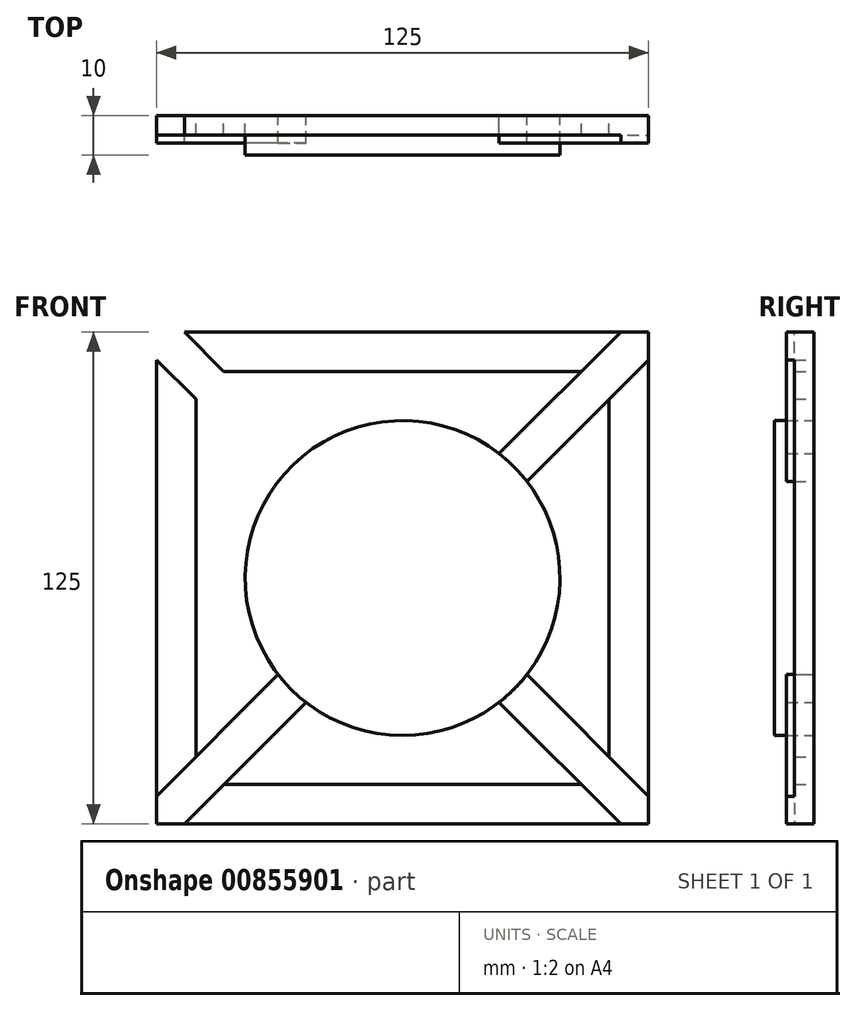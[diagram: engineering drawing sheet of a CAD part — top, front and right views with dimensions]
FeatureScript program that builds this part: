
annotation { "Feature Type Name" : "Feature", "Feature Type Description" : "" }
export const myFeature = defineFeature(function(context is Context, id is Id, definition is map)
    precondition{}
    {
        {
            var Q0;
            Q0=qCreatedBy(makeId("Front.planeOp"),FACE);
            var sketch = newSketch(context, id + "F0", { "sketchPlane" : qUnion([Q0])});
            skLineSegment(sketch, "E0", {"start": v(50.2, 9.17) * mm, "end": v(50.2, -90.83) * mm});
            skLineSegment(sketch, "E1", {"start": v(50.2, -90.83) * mm, "end": v(-74.8, -90.83) * mm});
            skLineSegment(sketch, "E2", {"start": v(-74.8, -90.83) * mm, "end": v(-74.8, 34.17) * mm});
            skLineSegment(sketch, "E3", {"start": v(-74.8, 34.17) * mm, "end": v(50.2, 34.17) * mm});
            skLineSegment(sketch, "E4", {"start": v(50.2, 34.17) * mm, "end": v(50.2, 9.17) * mm});
            skPoint(sketch, "E5.endSnap0", {"position": v(-37.4, -38.1) * mm});
            skLineSegment(sketch, "E6", {"start": v(-74.8, -28.33) * mm, "end": v(-64.8, -28.33) * mm});
            skLineSegment(sketch, "E7", {"start": v(0, 34.17) * mm, "end": v(0, 24.17) * mm});
            skLineSegment(sketch, "E8", {"start": v(0, -90.83) * mm, "end": v(0, -80.83) * mm});
            skLineSegment(sketch, "E9", {"start": v(50.2, 0) * mm, "end": v(40.2, 0) * mm});
            skLineSegment(sketch, "E10", {"start": v(-12.3, -28.33) * mm, "end": v(-12.3, 34.17) * mm});
            skCircle(sketch, "E11", {"center": v(-12.3, -28.33) * mm, "radius": 40 * mm});
            skPoint(sketch, "E12.endSnap0", {"position": v(25.1, -80.83) * mm});
            skLineSegment(sketch, "E13", {"start": v(-44.16, 3.54) * mm, "end": v(-40.63, 7.07) * mm});
            skLineSegment(sketch, "E14", {"start": v(-44.16, 3.54) * mm, "end": v(-47.7, 0) * mm});
            skLineSegment(sketch, "E15", {"start": v(-44.16, -60.2) * mm, "end": v(-40.63, -63.74) * mm});
            skLineSegment(sketch, "E16", {"start": v(-44.16, -60.2) * mm, "end": v(-47.7, -56.67) * mm});
            skLineSegment(sketch, "E17", {"start": v(28.89, -69.52) * mm, "end": v(25.35, -73.05) * mm});
            skLineSegment(sketch, "E18", {"start": v(28.89, -69.52) * mm, "end": v(32.42, -65.98) * mm});
            skLineSegment(sketch, "E19", {"start": v(27.75, 11.72) * mm, "end": v(31.3, 8.18) * mm});
            skLineSegment(sketch, "E20", {"start": v(27.75, 11.72) * mm, "end": v(24.22, 15.25) * mm});
            skLineSegment(sketch, "E21", {"start": v(-40.63, -63.74) * mm, "end": v(-67.72, -90.83) * mm});
            skLineSegment(sketch, "E22", {"start": v(-47.7, -56.67) * mm, "end": v(-74.8, -83.76) * mm});
            skLineSegment(sketch, "E23", {"start": v(25.35, -73.05) * mm, "end": v(43.13, -90.83) * mm});
            skLineSegment(sketch, "E24", {"start": v(32.42, -65.98) * mm, "end": v(50.2, -83.76) * mm});
            skLineSegment(sketch, "E25", {"start": v(31.3, 8.18) * mm, "end": v(19.3, -3.8) * mm});
            skLineSegment(sketch, "E26", {"start": v(31.3, 8.18) * mm, "end": v(50.2, 27.1) * mm});
            skLineSegment(sketch, "E27", {"start": v(24.22, 15.25) * mm, "end": v(12.23, 3.27) * mm});
            skLineSegment(sketch, "E28", {"start": v(24.22, 15.25) * mm, "end": v(43.13, 34.17) * mm});
            skLineSegment(sketch, "E29", {"start": v(-47.7, -56.67) * mm, "end": v(-43.9, -52.86) * mm});
            skLineSegment(sketch, "E30", {"start": v(-40.63, -63.74) * mm, "end": v(-36.82, -59.93) * mm});
            skLineSegment(sketch, "E31", {"start": v(32.42, -65.98) * mm, "end": v(19.3, -52.86) * mm});
            skLineSegment(sketch, "E32", {"start": v(25.35, -73.05) * mm, "end": v(12.23, -59.93) * mm});
            skLineSegment(sketch, "E33", {"start": v(-47.7, 0) * mm, "end": v(-74.8, 27.1) * mm});
            skLineSegment(sketch, "E34", {"start": v(-40.63, 7.07) * mm, "end": v(-67.72, 34.17) * mm});
            skLineSegment(sketch, "E35", {"start": v(-47.7, 0) * mm, "end": v(-40.63, 7.07) * mm});
            skLineSegment(sketch, "E36", {"start": v(-40.63, 7.07) * mm, "end": v(-36.82, 3.27) * mm});
            skLineSegment(sketch, "E37", {"start": v(-64.8, -28.33) * mm, "end": v(-64.8, 17.1) * mm});
            skLineSegment(sketch, "E38", {"start": v(-64.8, -28.33) * mm, "end": v(-64.8, -73.76) * mm});
            skLineSegment(sketch, "E39", {"start": v(0, -80.83) * mm, "end": v(-57.72, -80.83) * mm});
            skLineSegment(sketch, "E40", {"start": v(0, -80.83) * mm, "end": v(33.13, -80.83) * mm});
            skLineSegment(sketch, "E41", {"start": v(40.2, 0) * mm, "end": v(40.2, -73.76) * mm});
            skLineSegment(sketch, "E42", {"start": v(40.2, 0) * mm, "end": v(40.2, 17.1) * mm});
            skLineSegment(sketch, "E43", {"start": v(0, 24.17) * mm, "end": v(33.13, 24.17) * mm});
            skLineSegment(sketch, "E44", {"start": v(0, 24.17) * mm, "end": v(-57.72, 24.17) * mm});
            skLineSegment(sketch, "E45", {"start": v(-44.16, -3.54) * mm, "end": v(-43.9, -3.8) * mm});
            skLineSegment(sketch, "E46", {"start": v(-43.9, -3.8) * mm, "end": v(-43.9, -3.8) * mm});
            skLineSegment(sketch, "E47", {"start": v(-47.7, 0) * mm, "end": v(-44.16, -3.54) * mm});
            skSolve(sketch);
        }
        {
            var Q0;
            {var subQ0=sQuery(id+"F0.wireOp",EDGE,"E11");var subQ5=makeQuery(id+"F0.imprint","INTERSECT",VERTEX,{"derivedFrom":[subQ0,sQuery(id+"F0.wireOp",EDGE,"E25")]});Q0=makeQuery(id+"F0.imprint","IMPRINT",FACE,{"disambiguationData":[TD([[makeQuery(id+"F0.imprint","IMPRINT",EDGE,{"disambiguationData":[TD([[subQ5,-1.0]])],"derivedFrom":subQ0}),1.0]])]});}
            extrude(context, id + "F1", {"entities" : qUnion([Q0]), "depth" : 10 * mm, "offsetDistance" : 25 * mm});
        }
        {
            var Q0;
            {var subQ4=sQuery(id+"F0.wireOp",EDGE,"E35");Q0=makeQuery(id+"F0.imprint","IMPRINT",FACE,{"disambiguationData":[TD([[makeQuery(id+"F0.imprint","IMPRINT",EDGE,{"derivedFrom":subQ4}),1.0]])]});}
            var Q1;
            Q1=makeQuery(id+"F0.imprint","IMPRINT",FACE,{"disambiguationData":[TD([[makeQuery(id+"F0.imprint","IMPRINT",EDGE,{"derivedFrom":sQuery(id+"F0.wireOp",EDGE,"E35")}),-1.0]])]});
            var Q2;
            {var subQ1=sQuery(id+"F0.wireOp",EDGE,"E15");Q2=makeQuery(id+"F0.imprint","IMPRINT",FACE,{"disambiguationData":[TD([[makeQuery(id+"F0.imprint","IMPRINT",EDGE,{"derivedFrom":subQ1}),-1.0]])]});}
            var Q3;
            Q3=makeQuery(id+"F0.imprint","IMPRINT",FACE,{"disambiguationData":[TD([[makeQuery(id+"F0.imprint","IMPRINT",EDGE,{"derivedFrom":sQuery(id+"F0.wireOp",EDGE,"E15")}),1.0]])]});
            var Q4;
            {var subQ7=sQuery(id+"F0.wireOp",EDGE,"E19");Q4=makeQuery(id+"F0.imprint","IMPRINT",FACE,{"disambiguationData":[TD([[makeQuery(id+"F0.imprint","IMPRINT",EDGE,{"derivedFrom":subQ7}),1.0]])]});}
            var Q5;
            Q5=makeQuery(id+"F0.imprint","IMPRINT",FACE,{"disambiguationData":[TD([[makeQuery(id+"F0.imprint","IMPRINT",EDGE,{"derivedFrom":sQuery(id+"F0.wireOp",EDGE,"E19")}),-1.0]])]});
            var Q6;
            {var subQ6=sQuery(id+"F0.wireOp",EDGE,"E17");Q6=makeQuery(id+"F0.imprint","IMPRINT",FACE,{"disambiguationData":[TD([[makeQuery(id+"F0.imprint","IMPRINT",EDGE,{"derivedFrom":subQ6}),1.0]])]});}
            var Q7;
            Q7=makeQuery(id+"F0.imprint","IMPRINT",FACE,{"disambiguationData":[TD([[makeQuery(id+"F0.imprint","IMPRINT",EDGE,{"derivedFrom":sQuery(id+"F0.wireOp",EDGE,"E17")}),-1.0]])]});
            extrude(context, id + "F2", {"entities" : qUnion([Q0, Q1, Q2, Q3, Q4, Q5, Q6, Q7]), "operationType" : NewBodyOperationType.ADD, "depth" : 7 * mm, "offsetDistance" : 25 * mm});
        }
        {
            var Q0;
            {var subQ0=sQuery(id+"F0.wireOp",EDGE,"E9");Q0=makeQuery(id+"F0.imprint","IMPRINT",FACE,{"disambiguationData":[TD([[makeQuery(id+"F0.imprint","IMPRINT",EDGE,{"derivedFrom":subQ0}),1.0]])]});}
            var Q1;
            {var subQ4=sQuery(id+"F0.wireOp",EDGE,"E9");Q1=makeQuery(id+"F0.imprint","IMPRINT",FACE,{"disambiguationData":[TD([[makeQuery(id+"F0.imprint","IMPRINT",EDGE,{"derivedFrom":subQ4}),-1.0]])]});}
            var Q2;
            {var subQ0=sQuery(id+"F0.wireOp",EDGE,"E7");Q2=makeQuery(id+"F0.imprint","IMPRINT",FACE,{"disambiguationData":[TD([[makeQuery(id+"F0.imprint","IMPRINT",EDGE,{"derivedFrom":subQ0}),1.0]])]});}
            var Q3;
            {var subQ0=sQuery(id+"F0.wireOp",EDGE,"E7");Q3=makeQuery(id+"F0.imprint","IMPRINT",FACE,{"disambiguationData":[TD([[makeQuery(id+"F0.imprint","IMPRINT",EDGE,{"derivedFrom":subQ0}),-1.0]])]});}
            var Q4;
            {var subQ0=sQuery(id+"F0.wireOp",EDGE,"E10");var subQ1=sQuery(id+"F0.wireOp",EDGE,"E3");var subQ2=makeQuery(id+"F0.imprint","INTERSECT",VERTEX,{"derivedFrom":[subQ1,subQ0]});Q4=makeQuery(id+"F0.imprint","IMPRINT",FACE,{"disambiguationData":[TD([[makeQuery(id+"F0.imprint","IMPRINT",EDGE,{"disambiguationData":[TD([[subQ2,1.0]])],"derivedFrom":subQ1}),-1.0]])]});}
            var Q5;
            {var subQ0=sQuery(id+"F0.wireOp",EDGE,"E6");Q5=makeQuery(id+"F0.imprint","IMPRINT",FACE,{"disambiguationData":[TD([[makeQuery(id+"F0.imprint","IMPRINT",EDGE,{"derivedFrom":subQ0}),1.0]])]});}
            var Q6;
            {var subQ0=sQuery(id+"F0.wireOp",EDGE,"E6");Q6=makeQuery(id+"F0.imprint","IMPRINT",FACE,{"disambiguationData":[TD([[makeQuery(id+"F0.imprint","IMPRINT",EDGE,{"derivedFrom":subQ0}),-1.0]])]});}
            var Q7;
            {var subQ0=sQuery(id+"F0.wireOp",EDGE,"E8");Q7=makeQuery(id+"F0.imprint","IMPRINT",FACE,{"disambiguationData":[TD([[makeQuery(id+"F0.imprint","IMPRINT",EDGE,{"derivedFrom":subQ0}),1.0]])]});}
            var Q8;
            {var subQ0=sQuery(id+"F0.wireOp",EDGE,"E8");Q8=makeQuery(id+"F0.imprint","IMPRINT",FACE,{"disambiguationData":[TD([[makeQuery(id+"F0.imprint","IMPRINT",EDGE,{"derivedFrom":subQ0}),-1.0]])]});}
            extrude(context, id + "F3", {"entities" : qUnion([Q0, Q1, Q2, Q3, Q4, Q5, Q6, Q7, Q8]), "operationType" : NewBodyOperationType.ADD, "depth" : 5 * mm, "offsetDistance" : 25 * mm});
        }
    });
